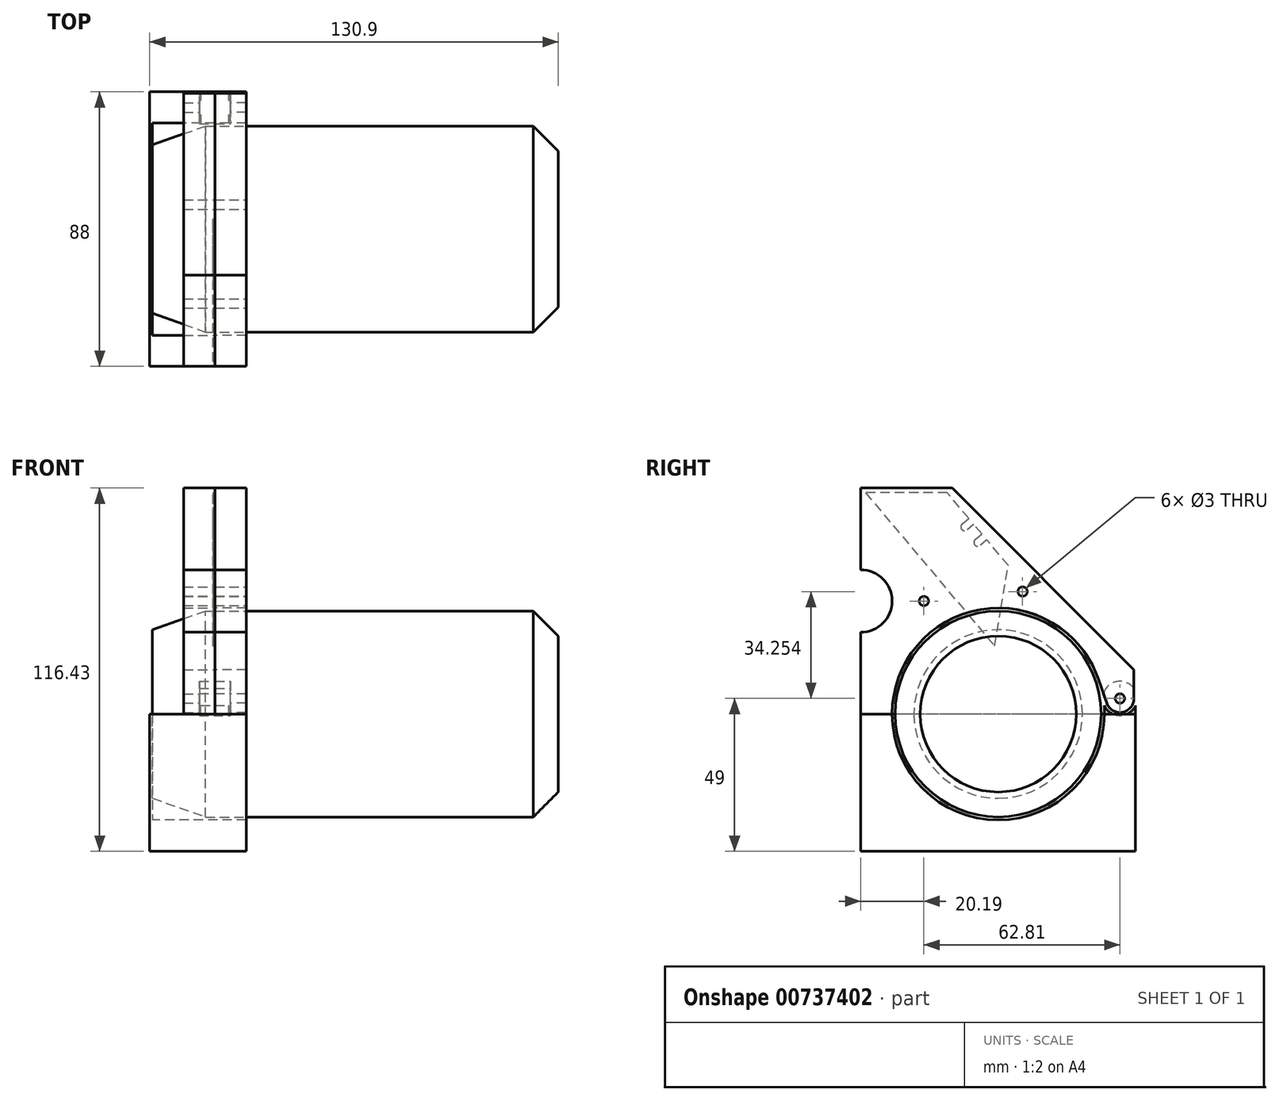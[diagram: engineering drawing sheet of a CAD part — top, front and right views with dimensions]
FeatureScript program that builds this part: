
annotation { "Feature Type Name" : "Feature", "Feature Type Description" : "" }
export const myFeature = defineFeature(function(context is Context, id is Id, definition is map)
    precondition{}
    {
        {
            var Q0;
            Q0=qCreatedBy(makeId("Front.planeOp"),FACE);
            var sketch = newSketch(context, id + "F0", { "sketchPlane" : qUnion([Q0])});
            skLineSegment(sketch, "E0", {"start": v(-20, 0) * mm, "end": v(-20, 27) * mm});
            skLineSegment(sketch, "E1", {"start": v(-20, 27) * mm, "end": v(-3, 33) * mm});
            skLineSegment(sketch, "E2", {"start": v(102, 33) * mm, "end": v(-3, 33) * mm});
            skLineSegment(sketch, "E3", {"start": v(102, 33) * mm, "end": v(110, 25) * mm});
            skLineSegment(sketch, "E4", {"start": v(110, 25) * mm, "end": v(110, 0) * mm});
            skLineSegment(sketch, "E5", {"start": v(110, 0) * mm, "end": v(-20, 0) * mm});
            skSolve(sketch);
        }
        {
            var Q0;
            Q0=makeQuery(id+"F0.imprint","IMPRINT",FACE,{"disambiguationData":[TD([[makeQuery(id+"F0.imprint","IMPRINT",EDGE,{"derivedFrom":sQuery(id+"F0.wireOp",EDGE,"E0")}),-1.0]])]});
            var Q1;
            Q1=sQuery(id+"F0.wireOp",EDGE,"E5");
            revolve(context, id + "F1", {"surfaceOperationType" : NewSurfaceOperationType.NEW, "entities" : qUnion([Q0]), "axis" : qUnion([Q1]), "revolveType" : RevolveType.FULL});
        }
        {
            var Q0;
            Q0=qCreatedBy(makeId("Right.planeOp"),FACE);
            var sketch = newSketch(context, id + "F2", { "sketchPlane" : qUnion([Q0])});
            skLineSegment(sketch, "E6", {"start": v(2.74, 47.48) * mm, "end": v(-1.49, 23) * mm});
            skLineSegment(sketch, "E7", {"start": v(-1.49, 23) * mm, "end": v(-41.43, 70.43) * mm});
            skLineSegment(sketch, "E8", {"start": v(-41.43, 70.43) * mm, "end": v(-16.59, 70.43) * mm});
            skLineSegment(sketch, "E9", {"start": v(-16.59, 70.43) * mm, "end": v(-10.15, 62.78) * mm});
            skArc(sketch, "E10", {"start": v(-7.68, 56.36) * mm, "mid": v(-7.9, 53.9) * mm, "end": v(-5.43, 53.68) * mm});
            skArc(sketch, "E11", {"start": v(-11.87, 61.33) * mm, "mid": v(-12.08, 58.86) * mm, "end": v(-9.61, 58.65) * mm});
            skLineSegment(sketch, "E12", {"start": v(-6.92, 58.95) * mm, "end": v(-21.46, 46.71) * mm, "construction": true});
            skLineSegment(sketch, "E13", {"start": v(-6.55, 55.02) * mm, "end": v(-10.74, 59.99) * mm, "construction": true});
            skLineSegment(sketch, "E14", {"start": v(-5.43, 53.68) * mm, "end": v(-3.7, 55.13) * mm});
            skLineSegment(sketch, "E15", {"start": v(-7.68, 56.36) * mm, "end": v(-5.96, 57.8) * mm});
            skLineSegment(sketch, "E16.trimOffspring", {"start": v(-3.7, 55.13) * mm, "end": v(2.74, 47.48) * mm});
            skLineSegment(sketch, "E17", {"start": v(-9.61, 58.65) * mm, "end": v(-7.9, 60.1) * mm});
            skLineSegment(sketch, "E18", {"start": v(-11.87, 61.33) * mm, "end": v(-10.15, 62.78) * mm});
            skLineSegment(sketch, "E19.trimOffspring", {"start": v(-7.9, 60.1) * mm, "end": v(-5.96, 57.8) * mm});
            skSolve(sketch);
        }
        {
            var Q0;
            Q0 = qSketchRegion(id + "F2", true);
            extrude(context, id + "F3", {"entities" : qUnion([Q0]), "oppositeDirection" : true, "depth" : 0.6 * mm, "offsetDistance" : 25 * mm});
        }
        {
            var Q0;
            Q0=makeQuery(id+"F1.opRevolve","SWEPT_FACE",FACE,{"disambiguationData":[OSD([sQuery(id+"F0.wireOp",EDGE,"E0")])]});
            cPlane(context, id + "F4", {"entities" : qUnion([Q0]), "cplaneType" : CPlaneType.OFFSET, "offset" : 0 * mm, "width" : 150 * mm, "height" : 150 * mm});
        }
        {
            var Q0;
            Q0=qCreatedBy(id+"F4.planeOp",FACE);
            var sketch = newSketch(context, id + "F5", { "sketchPlane" : qUnion([Q0])});
            skArc(sketch, "E20", {"start": v(-34, 0) * mm, "mid": v(0, -34) * mm, "end": v(34, 0) * mm});
            skLineSegment(sketch, "E21", {"start": v(34, 0) * mm, "end": v(44, 0) * mm});
            skLineSegment(sketch, "E22", {"start": v(44, 0) * mm, "end": v(44, -44) * mm});
            skLineSegment(sketch, "E23", {"start": v(44, -44) * mm, "end": v(-44, -44) * mm});
            skLineSegment(sketch, "E24", {"start": v(-44, -44) * mm, "end": v(-44, 0) * mm});
            skLineSegment(sketch, "E25", {"start": v(-44, 0) * mm, "end": v(-34, 0) * mm});
            skLineSegment(sketch, "E26", {"start": v(-34, 0) * mm, "end": v(34, 0) * mm});
            skSolve(sketch);
        }
        {
            var Q0;
            Q0=makeQuery(id+"F5.imprint","IMPRINT",FACE,{"disambiguationData":[TD([[makeQuery(id+"F5.imprint","IMPRINT",EDGE,{"derivedFrom":sQuery(id+"F5.wireOp",EDGE,"E20")}),-1.0]])]});
            extrude(context, id + "F6", {"entities" : qUnion([Q0]), "oppositeDirection" : true, "depth" : 30 * mm, "offsetDistance" : 25 * mm});
        }
        {
            var Q0;
            Q0=makeQuery(id+"F5.imprint","IMPRINT",FACE,{"disambiguationData":[TD([[makeQuery(id+"F5.imprint","IMPRINT",EDGE,{"derivedFrom":sQuery(id+"F5.wireOp",EDGE,"E20")}),1.0]])]});
            var Q1;
            Q1=makeQuery(id+"F5.imprint","IMPRINT",FACE,{"disambiguationData":[TD([[makeQuery(id+"F5.imprint","IMPRINT",EDGE,{"derivedFrom":sQuery(id+"F5.wireOp",EDGE,"E20")}),-1.0]])]});
            extrude(context, id + "F7", {"entities" : qUnion([Q0, Q1]), "operationType" : NewBodyOperationType.ADD, "depth" : 0.9 * mm, "offsetDistance" : 25 * mm});
        }
        {
            var Q0;
            Q0=qCreatedBy(makeId("Right.planeOp"),FACE);
            var sketch = newSketch(context, id + "F8", { "sketchPlane" : qUnion([Q0])});
            skLineSegment(sketch, "E27", {"start": v(44, 0) * mm, "end": v(34, 0) * mm});
            skArc(sketch, "E28", {"start": v(44, 5) * mm, "mid": v(39, 10) * mm, "end": v(34, 5) * mm});
            skLineSegment(sketch, "E29", {"start": v(44, 0) * mm, "end": v(44, 5) * mm});
            skLineSegment(sketch, "E30", {"start": v(34, 0) * mm, "end": v(34, 5) * mm});
            skCircle(sketch, "E31", {"center": v(39, 5) * mm, "radius": 1.5 * mm});
            skSolve(sketch);
        }
        {
            var Q0;
            Q0=makeQuery(id+"F8.imprint","IMPRINT",FACE,{"disambiguationData":[TD([[makeQuery(id+"F8.imprint","IMPRINT",EDGE,{"derivedFrom":sQuery(id+"F8.wireOp",EDGE,"E27")}),-1.0]])]});
            extrude(context, id + "F9", {"entities" : qUnion([Q0]), "operationType" : NewBodyOperationType.ADD, "depth" : 4.5 * mm, "offsetDistance" : 25 * mm, "hasSecondDirection" : true, "secondDirectionOppositeDirection" : true, "secondDirectionDepth" : 4.5 * mm});
        }
        {
            var Q0;
            Q0=qCreatedBy(makeId("Right.planeOp"),FACE);
            var sketch = newSketch(context, id + "F10", { "sketchPlane" : qUnion([Q0])});
            skLineSegment(sketch, "E32", {"start": v(-44, 0) * mm, "end": v(-44, 72.43) * mm});
            skLineSegment(sketch, "E33", {"start": v(-44, 72.43) * mm, "end": v(-14.73, 72.43) * mm});
            skCircle(sketch, "E34", {"center": v(39, 5) * mm, "radius": 4.5 * mm});
            skCircle(sketch, "E35", {"center": v(39, 5) * mm, "radius": 1.5 * mm});
            skArc(sketch, "E36", {"start": v(32.14, 11.08) * mm, "mid": v(-5.62, 33.53) * mm, "end": v(-34, 0) * mm});
            skLineSegment(sketch, "E37", {"start": v(34.75, 3.53) * mm, "end": v(32.14, 11.08) * mm});
            skLineSegment(sketch, "E38", {"start": v(-44, 0) * mm, "end": v(-34, 0) * mm});
            skLineSegment(sketch, "E39", {"start": v(43.5, 5) * mm, "end": v(43.5, 14.2) * mm});
            skLineSegment(sketch, "E40", {"start": v(43.5, 14.2) * mm, "end": v(-14.73, 72.43) * mm});
            skSolve(sketch);
        }
        {
            var Q0;
            Q0=makeQuery(id+"F10.imprint","IMPRINT",FACE,{"disambiguationData":[TD([[makeQuery(id+"F10.imprint","IMPRINT",EDGE,{"derivedFrom":sQuery(id+"F10.wireOp",EDGE,"E32")}),-1.0]])]});
            var Q1;
            Q1=makeQuery(id+"F10.imprint","IMPRINT",FACE,{"disambiguationData":[TD([[makeQuery(id+"F10.imprint","IMPRINT",EDGE,{"derivedFrom":sQuery(id+"F10.wireOp",EDGE,"E35")}),-1.0]])]});
            extrude(context, id + "F11", {"entities" : qUnion([Q0, Q1]), "oppositeDirection" : true, "depth" : 10 * mm, "offsetDistance" : 25 * mm});
        }
        {
            var Q0;
            Q0=qCreatedBy(makeId("Right.planeOp"),FACE);
            var sketch = newSketch(context, id + "F12", { "sketchPlane" : qUnion([Q0])});
            skLineSegment(sketch, "E41.0", {"start": v(-3.64, 55.83) * mm, "end": v(-5.75, 54.06) * mm});
            skArc(sketch, "E41.1", {"start": v(-9.93, 59.03) * mm, "mid": v(-11.7, 59.18) * mm, "end": v(-11.54, 60.95) * mm});
            skLineSegment(sketch, "E41.2", {"start": v(-7.83, 60.8) * mm, "end": v(-9.93, 59.03) * mm});
            skLineSegment(sketch, "E41.3", {"start": v(-5.25, 57.74) * mm, "end": v(-7.83, 60.8) * mm});
            skLineSegment(sketch, "E41.4", {"start": v(-7.36, 55.97) * mm, "end": v(-5.25, 57.74) * mm});
            skLineSegment(sketch, "E41.5", {"start": v(-11.54, 60.95) * mm, "end": v(-9.44, 62.72) * mm});
            skArc(sketch, "E41.6", {"start": v(-5.75, 54.06) * mm, "mid": v(-7.5, 54.21) * mm, "end": v(-7.36, 55.97) * mm});
            skLineSegment(sketch, "E41.7", {"start": v(-9.44, 62.72) * mm, "end": v(-16.35, 70.93) * mm});
            skLineSegment(sketch, "E41.8", {"start": v(-16.35, 70.93) * mm, "end": v(-42.5, 70.93) * mm});
            skLineSegment(sketch, "E41.9", {"start": v(-42.5, 70.93) * mm, "end": v(-1.18, 21.86) * mm});
            skLineSegment(sketch, "E41.10", {"start": v(-1.18, 21.86) * mm, "end": v(3.27, 47.62) * mm});
            skLineSegment(sketch, "E41.11", {"start": v(3.27, 47.62) * mm, "end": v(-3.64, 55.83) * mm});
            skLineSegment(sketch, "E42.2", {"start": v(-39, 5) * mm, "end": v(-38.68, 5) * mm});
            skCircle(sketch, "E43", {"center": v(39, 5) * mm, "radius": 5.5 * mm});
            skCircle(sketch, "E44", {"center": v(-44, 36.21) * mm, "radius": 10 * mm});
            skCircle(sketch, "E45", {"center": v(-23.8, 36.21) * mm, "radius": 1.5 * mm});
            skCircle(sketch, "E46", {"center": v(7.81, 39.25) * mm, "radius": 1.5 * mm});
            skSolve(sketch);
        }
        {
            var Q0;
            Q0=makeQuery(id+"F12.imprint","IMPRINT",FACE,{"disambiguationData":[TD([[makeQuery(id+"F12.imprint","IMPRINT",EDGE,{"derivedFrom":sQuery(id+"F12.wireOp",EDGE,"E41.0")}),1.0]])]});
            extrude(context, id + "F13", {"entities" : qUnion([Q0]), "operationType" : NewBodyOperationType.REMOVE, "oppositeDirection" : true, "depth" : 0.6 * mm, "offsetDistance" : 25 * mm});
        }
        {
            var Q0;
            Q0=makeQuery(id+"F10.imprint","IMPRINT",FACE,{"disambiguationData":[TD([[makeQuery(id+"F10.imprint","IMPRINT",EDGE,{"derivedFrom":sQuery(id+"F10.wireOp",EDGE,"E32")}),-1.0]])]});
            var Q1;
            Q1=makeQuery(id+"F10.imprint","IMPRINT",FACE,{"disambiguationData":[TD([[makeQuery(id+"F10.imprint","IMPRINT",EDGE,{"derivedFrom":sQuery(id+"F10.wireOp",EDGE,"E35")}),-1.0]])]});
            extrude(context, id + "F14", {"entities" : qUnion([Q0, Q1]), "depth" : 10 * mm, "offsetDistance" : 25 * mm});
        }
        {
            var Q0;
            Q0=makeQuery(id+"F12.imprint","IMPRINT",FACE,{"disambiguationData":[TD([[makeQuery(id+"F12.imprint","IMPRINT",EDGE,{"derivedFrom":sQuery(id+"F12.wireOp",EDGE,"E43")}),1.0]])]});
            extrude(context, id + "F15", {"entities" : qUnion([Q0]), "operationType" : NewBodyOperationType.REMOVE, "oppositeDirection" : true, "depth" : 5 * mm, "offsetDistance" : 25 * mm, "hasSecondDirection" : true, "secondDirectionOppositeDirection" : false, "secondDirectionDepth" : 5 * mm});
        }
        {
            var Q0;
            Q0=makeQuery(id+"F12.imprint","IMPRINT",FACE,{"disambiguationData":[TD([[makeQuery(id+"F12.imprint","IMPRINT",EDGE,{"derivedFrom":sQuery(id+"F12.wireOp",EDGE,"E44")}),1.0]])]});
            var Q1;
            Q1=makeQuery(id+"F12.imprint","IMPRINT",FACE,{"disambiguationData":[TD([[makeQuery(id+"F12.imprint","IMPRINT",EDGE,{"derivedFrom":sQuery(id+"F12.wireOp",EDGE,"E45")}),1.0]])]});
            var Q2;
            Q2=makeQuery(id+"F12.imprint","IMPRINT",FACE,{"disambiguationData":[TD([[makeQuery(id+"F12.imprint","IMPRINT",EDGE,{"derivedFrom":sQuery(id+"F12.wireOp",EDGE,"E46")}),1.0]])]});
            extrude(context, id + "F16", {"entities" : qUnion([Q0, Q1, Q2]), "operationType" : NewBodyOperationType.REMOVE, "endBound" : BoundingType.THROUGH_ALL, "oppositeDirection" : true, "depth" : 25 * mm, "offsetDistance" : 25 * mm, "hasSecondDirection" : true, "secondDirectionBound" : SecondDirectionBoundingType.THROUGH_ALL, "secondDirectionOppositeDirection" : false, "secondDirectionDepth" : 25 * mm});
        }
    });
